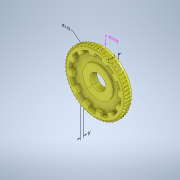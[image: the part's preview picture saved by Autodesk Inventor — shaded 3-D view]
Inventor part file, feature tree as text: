
AUTODESK INVENTOR PART (.ipt)
format: ipt  version: 2022.2 (Build 262287010, 287A)  size: 1,359,360 bytes
history: native  units: mm (DEFAULTED — no unit token found)
features: other x25, sketch x7, extrude x6, plane x3, pattern_circular x2
ambient origin geometry x5: Origin, X Axis, Y Axis, Z Axis, Center Point
bodies: Solid1 (feature_tree)
feature tree (43):
  other  "Annotations"
  other  "Tooth Plane"
  other  "Base Body Sketch"
  other  "Base Body"
  other  "Base Body2"
  plane  "Work Plane13"
  other  "Tooth"
  pattern_circular  "Tooth Pattern"  Angle=90.0deg  [1 undecoded]
  plane  "Work Plane14"
  plane  "Work Plane15"
  extrude  "Extrusion2"  Depth=6.35mm
  extrude  "Extrusion3"  TaperAngle=360.0deg  [1 undecoded]
  extrude  "Extrusion7"  Depth=6.35mm
  pattern_circular  "Circular Pattern7"  [2 undecoded]
  extrude  "Extrusion8"  Depth=6.35mm TaperAngle=0.0deg
  extrude  "Extrusion9"  Depth=6.35mm
  extrude  "Extrusion10"  Depth=6.35mm
  other  "Tooth Sketch"
  sketch  "Sketch8"  dims[d35=90.0deg]
  other  "Srf1"
  sketch  "Sketch10"  dims[d37=-0.996687mm]
  sketch  "Sketch11"  dims[d38=56.595498mm]
  sketch  "Sketch16"  dims[d39=3.490659mm]
  other  "Work Axis2"
  other  "Work Axis3"
  other  "Work Axis4"
  other  "Work Axis5"
  other  "Work Axis6"
  other  "Work Axis7"
  other  "Work Axis8"
  other  "Work Axis9"
  other  "Work Axis10"
  other  "Work Axis11"
  other  "Work Axis12"
  sketch  "Sketch17"  dims[d40=6.144654mm]
  sketch  "Sketch18"  dims[d41=8.085071mm]
  sketch  "Sketch19"  dims[d42=1.524mm d43=90.0deg d44=600.0mm d46=360.0deg d50=5.130925mm d68=56.595498mm d69=0.0mm d73=0.0mm d75=0.523599mm d77=97.020853mm d78=9.525mm d79=0.0mm d80=0.0mm d81=0.0mm d82=0.0mm d83=0.523599mm d84=0.0mm d85=180.0deg d86=56.595498mm d87=101.871896mm d89=12.936114mm d90=90.0deg d92=9.525mm d93=56.595498mm d97=76.3905mm d98=0.0mm d99=0.0mm d102=25.781mm d103=94.869mm d104=6.35mm d105=0.0mm d151=0.087266mm d152=2.792527mm d153=5.177778mm d154=9.525mm d155=0.0mm d156=120.0mm d157=360.0deg d159=76.3905mm d160=86.746057mm d168=50.8mm d169=4.7625mm d170=0.0mm d171=88.9mm d172=5.08mm d173=5.08mm d174=2.54mm d175=0.0mm d180=3.175mm d181=0.0mm d161=16.054975mm d162=94.869mm d163=2.141741mm d164=8.066574mm d165=6.35mm d166=6.656436mm d167=25.781mm d177=7.715547mm d178=7.103274mm d179=9.525mm d182=2.118813mm d183=6.920726mm d184=6.35mm]
  other  "Pitch Diameter"
  other  "Diameter Dimension 1"
  other  "Linear Dimension 1"
  other  "Diameter Dimension 2"
  other  "Linear Dimension 2"
  other  "Linear Dimension 3"
note: 4 required parameter values undecoded (feature->parameter linkage not recoverable at this tier; creation-order binding heuristic only, values carry confidence <= 0.55)
